# Revit family: M_螢光燈管槽 - 拋物線狀矩形
name_source: partatom
category: Leuchten
revit_build: Autodesk Revit 2017 (Build: 20160109_1515(x64)
units: mm (PartAtom-declared; Revit-internal decimal feet)

## family parameters
Basisbauteil = Fläche
Beim Laden mit Abzugskörper schneiden = Nein
Bemaßung runder Anschluss = Durchmesser verwenden
Gemeinsam genutzt = Nein
Lichtquelle = Ja
OmniClass-Nummer = 23.80.70.11.14.11
OmniClass-Titel = Downlights
Raumberechnungspunkt = Nein
Teiletyp = Normal

## types (4) — shared parameters
Baugruppenkennzeichen = D5020210
Emissionsform beim Rendern sichtbar = Nein
Farbfilter = 16777215
Farbtemperaturverschiebung bei Dämpfen der Lampe = <Keine Auswahl>
Lampe = T-12
Neigungswinkel = -90.00°
Vorgabe-Ansicht = 1200 mm  [stored 3.93701 ft]
分佈口材料 = 玻璃，白色，高亮度
格線材料 = 鋼，油漆塗層，深灰，霧面
燈箱材料 = 鋼，鍍鉻
穩壓器極數 = 1
負載分類 = 照明 - 住宅單元

## per-type parameters (varying)
| type | Datei für fotometrisches Netz | Scheinlast | Von Breite des Rechtecks ausssenden | Von Länge des Rechtecks aussenden | 穩壓器電壓 |
| 0600x1200mm (2 燈) - 120V | 2x42T12.ies | 80 VA | 560 mm  [stored 1.83727 ft] | 1169 mm | 120 V |
| 0600x1200mm (2 燈) - 277V | 2x42T12.ies | 80 VA | 610 mm | 1219 mm | 277 V |
| 0600x1200mm (4 燈) - 120V | 2x44T12.ies | 160 VA | 610 mm | 1219 mm | 120 V |
| 0600x1200mm (4 燈) - 277V | 2x44T12.ies | 160 VA | 610 mm | 1219 mm | 277 V |

note: [stored X ft] marks values corroborated as IEEE doubles in the binary element streams (Revit-internal decimal feet)
